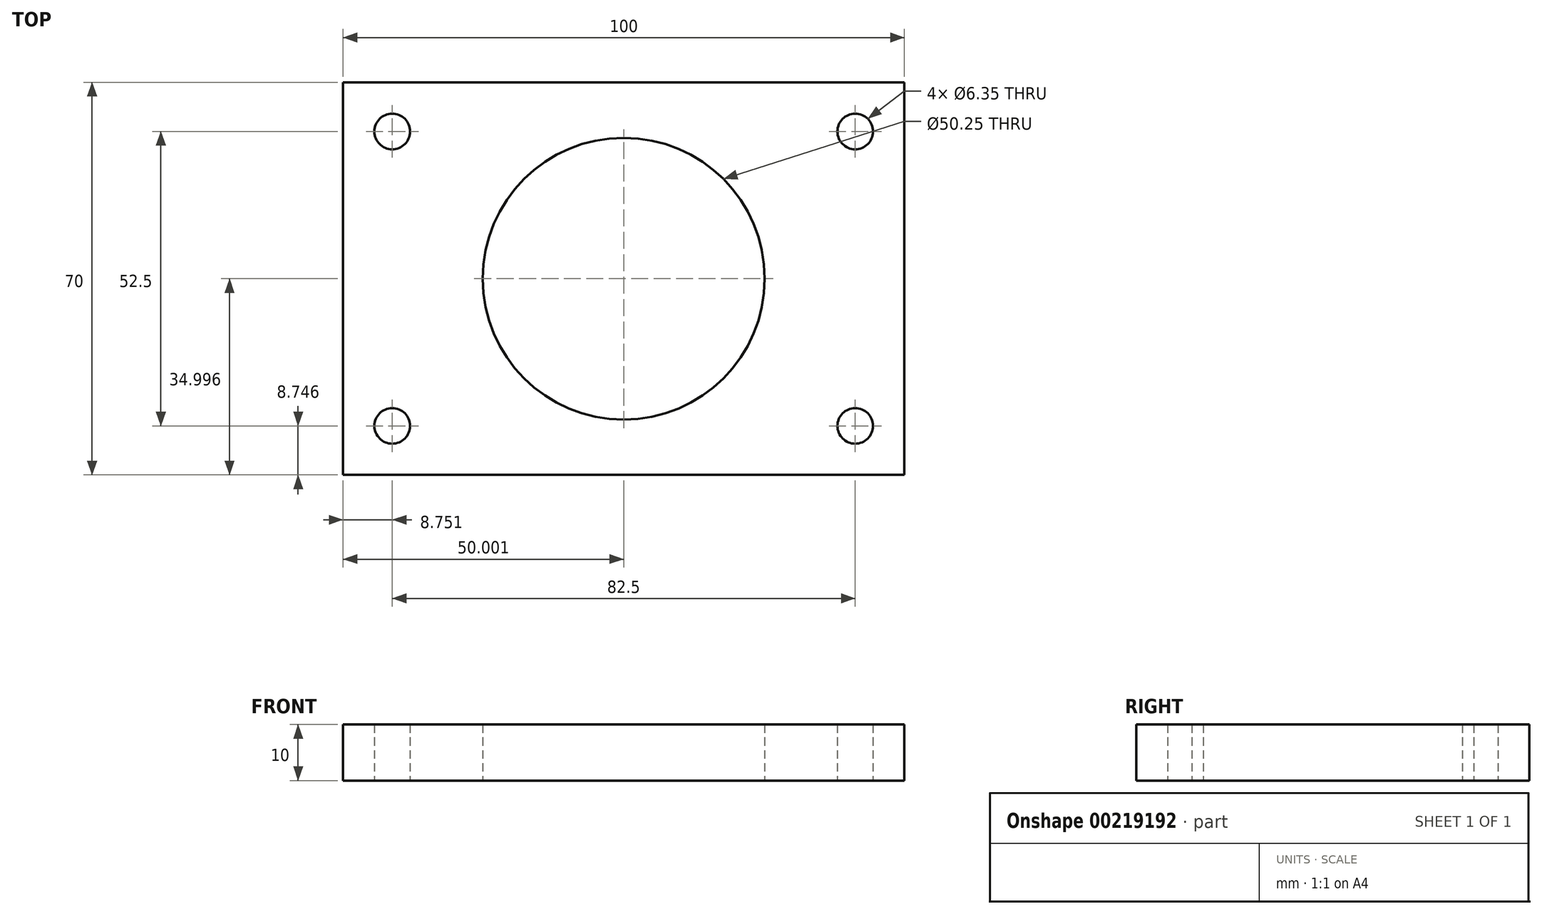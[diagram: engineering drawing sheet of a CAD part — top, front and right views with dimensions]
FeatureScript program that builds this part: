
annotation { "Feature Type Name" : "Feature", "Feature Type Description" : "" }
export const myFeature = defineFeature(function(context is Context, id is Id, definition is map)
    precondition{}
    {
        {
            var Q0;
            Q0=qCreatedBy(makeId("Top.planeOp"),FACE);
            var sketch = newSketch(context, id + "F0", { "sketchPlane" : qUnion([Q0])});
            skLineSegment(sketch, "E0", {"start": v(-47.02, 24.29) * mm, "end": v(-47.02, -45.71) * mm});
            skLineSegment(sketch, "E1", {"start": v(-47.02, -45.71) * mm, "end": v(52.98, -45.71) * mm});
            skLineSegment(sketch, "E2", {"start": v(52.98, -45.71) * mm, "end": v(52.98, 24.29) * mm});
            skLineSegment(sketch, "E3", {"start": v(52.98, 24.29) * mm, "end": v(-47.02, 24.29) * mm});
            skCircle(sketch, "E4", {"center": v(-38.27, 15.54) * mm, "radius": 3.18 * mm});
            skCircle(sketch, "E5", {"center": v(2.98, -10.71) * mm, "radius": 25.12 * mm});
            skCircle(sketch, "E6.MirrorC", {"center": v(44.23, 15.54) * mm, "radius": 3.18 * mm});
            skCircle(sketch, "E7.MirrorC", {"center": v(2.98, -10.71) * mm, "radius": 25 * mm});
            skCircle(sketch, "E8.MirrorC", {"center": v(44.23, -36.96) * mm, "radius": 3.18 * mm});
            skCircle(sketch, "E9.MirrorC", {"center": v(-38.27, -36.96) * mm, "radius": 3.18 * mm});
            skSolve(sketch);
        }
        {
            var Q0;
            Q0=makeQuery(id+"F0.imprint","IMPRINT",FACE,{"disambiguationData":[TD([[makeQuery(id+"F0.imprint","IMPRINT",EDGE,{"derivedFrom":sQuery(id+"F0.wireOp",EDGE,"E0")}),1.0]])]});
            extrude(context, id + "F1", {"entities" : qUnion([Q0]), "depth" : 10 * mm});
        }
    });
